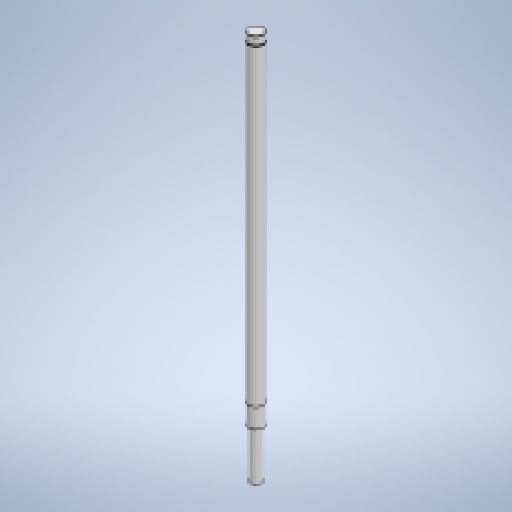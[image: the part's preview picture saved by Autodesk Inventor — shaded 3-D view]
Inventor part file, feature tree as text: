
AUTODESK INVENTOR PART (.ipt)
format: ipt  version: 2025 (Build 290162010, 162A)  size: 186,368 bytes
history: native  units: mm
features: sketch x2, revolve x1, plane x1, extrude x1, chamfer x1, projected_geometry x1
ambient origin geometry x8: Origin, YZ Plane, XZ Plane, XY Plane, X Axis, Y Axis, Z Axis, Center Point
bodies: Solid1 (feature_tree)
feature tree (7):
  revolve  "Revolution1"  [1 undecoded]
  plane  "Work Plane1"
  extrude  "Extrusion1"  TaperAngle=360.0deg  [1 undecoded]
  chamfer  "Chamfer1"  Distance=85.0mm
  sketch  "Sketch1"  dims[d0=25.0mm d1=280.0mm]
  sketch  "Sketch2"  dims[d2=395.0mm d3=360.0deg d4=85.0mm d5=18.0mm d6=24.0mm d7=35.0mm d8=15.0mm d9=1.595mm d10=78.0mm d11=63.0mm d12=6.0mm d13=3.5mm d14=0.0mm d15=1.0mm d16=2.0mm d17=45.0deg d18=22.0mm d19=2.0mm]
  projected_geometry  "Projected Loop1"
note: 2 required parameter values undecoded (feature->parameter linkage not recoverable at this tier; creation-order binding heuristic only, values carry confidence <= 0.55)